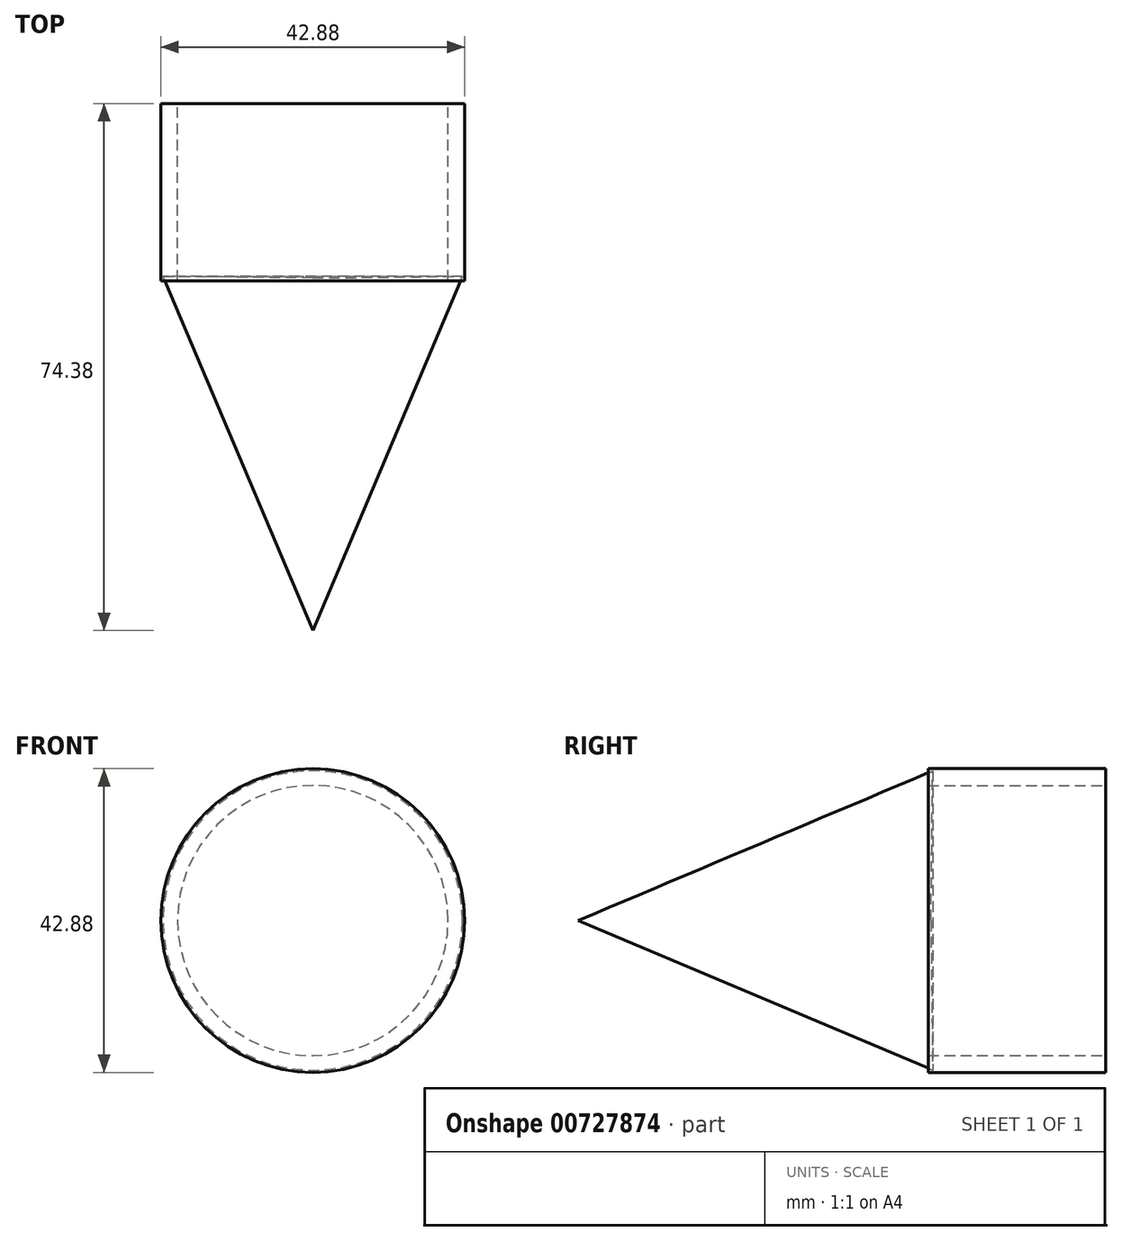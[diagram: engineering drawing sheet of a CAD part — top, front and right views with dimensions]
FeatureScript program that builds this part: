
annotation { "Feature Type Name" : "Feature", "Feature Type Description" : "" }
export const myFeature = defineFeature(function(context is Context, id is Id, definition is map)
    precondition{}
    {
        {
            var Q0;
            Q0=qCreatedBy(makeId("Front.planeOp"),FACE);
            var sketch = newSketch(context, id + "F0", { "sketchPlane" : qUnion([Q0])});
            skCircle(sketch, "E0", {"center": v(0, 0) * mm, "radius": 21.43 * mm});
            skCircle(sketch, "E1", {"center": v(0, 0) * mm, "radius": 19.08 * mm});
            skSolve(sketch);
        }
        {
            var Q0;
            Q0 = qSketchRegion(id + "F0", true);
            extrude(context, id + "F1", {"entities" : qUnion([Q0]), "depth" : 25 * mm, "offsetDistance" : 25 * mm});
        }
        {
            var Q0;
            Q0=qCreatedBy(makeId("Right.planeOp"),FACE);
            var sketch = newSketch(context, id + "F2", { "sketchPlane" : qUnion([Q0])});
            skLineSegment(sketch, "E2", {"start": v(-24.38, 21.12) * mm, "end": v(-74.38, 0) * mm});
            skLineSegment(sketch, "E3", {"start": v(-74.38, 0) * mm, "end": v(-24.63, 0) * mm});
            skLineSegment(sketch, "E4", {"start": v(-24.38, 21.12) * mm, "end": v(-24.63, 0) * mm});
            skLineSegment(sketch, "E5", {"start": v(0, 0) * mm, "end": v(-8.87, 0) * mm});
            skSolve(sketch);
        }
        {
            var Q0;
            Q0=makeQuery(id+"F2.imprint","IMPRINT",FACE,{"disambiguationData":[TD([[makeQuery(id+"F2.imprint","IMPRINT",EDGE,{"derivedFrom":sQuery(id+"F2.wireOp",EDGE,"E2")}),1.0]])]});
            var Q1;
            Q1=sQuery(id+"F2.wireOp",EDGE,"E5");
            revolve(context, id + "F3", {"surfaceOperationType" : NewSurfaceOperationType.NEW, "entities" : qUnion([Q0]), "axis" : qUnion([Q1]), "revolveType" : RevolveType.FULL});
        }
    });
